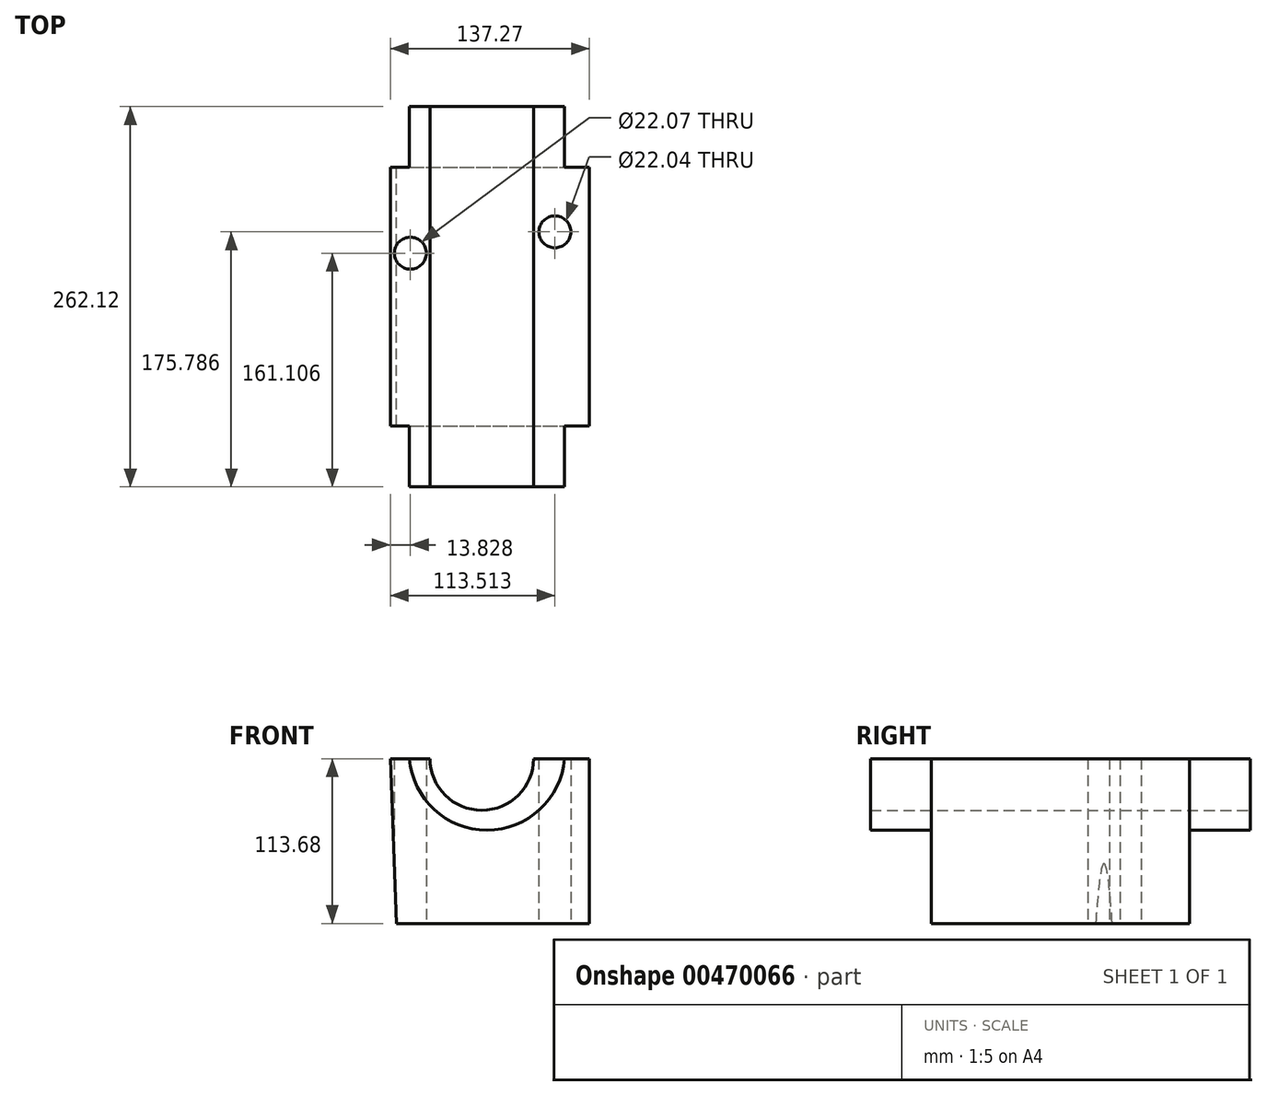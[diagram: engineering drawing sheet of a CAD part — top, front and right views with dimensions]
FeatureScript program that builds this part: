
annotation { "Feature Type Name" : "Feature", "Feature Type Description" : "" }
export const myFeature = defineFeature(function(context is Context, id is Id, definition is map)
    precondition{}
    {
        {
            var Q0;
            Q0=qCreatedBy(makeId("Front.planeOp"),FACE);
            var sketch = newSketch(context, id + "F0", { "sketchPlane" : qUnion([Q0])});
            skLineSegment(sketch, "E0", {"start": v(-69.6, -60) * mm, "end": v(63.28, -60) * mm});
            skLineSegment(sketch, "E1", {"start": v(63.28, -60) * mm, "end": v(63.28, 53.67) * mm});
            skLineSegment(sketch, "E2", {"start": v(63.28, 53.67) * mm, "end": v(24.9, 53.67) * mm});
            skLineSegment(sketch, "E3", {"start": v(-73.99, 53.67) * mm, "end": v(-69.6, -60) * mm});
            skArc(sketch, "E4", {"start": v(-46.69, 53.67) * mm, "mid": v(-10.9, 18.09) * mm, "end": v(24.9, 53.67) * mm});
            skArc(sketch, "E5", {"start": v(-60.81, 53.67) * mm, "mid": v(-7.3, 4.33) * mm, "end": v(46.22, 53.67) * mm});
            skLineSegment(sketch, "E6.trimOffspring", {"start": v(-46.69, 53.67) * mm, "end": v(-73.99, 53.67) * mm});
            skSolve(sketch);
        }
        {
            var Q0;
            Q0 = qSketchRegion(id + "F0", true);
            extrude(context, id + "F1", {"entities" : qUnion([Q0]), "endBound" : BoundingType.SYMMETRIC, "depth" : 178.3 * mm});
        }
        {
            var Q0;
            {var subQ0=sQuery(id+"F0.wireOp",EDGE,"E4");Q0=makeQuery(id+"F0.imprint","IMPRINT",FACE,{"disambiguationData":[TD([[makeQuery(id+"F0.imprint","IMPRINT",EDGE,{"derivedFrom":subQ0}),-1.0]])]});}
            extrude(context, id + "F2", {"entities" : qUnion([Q0]), "operationType" : NewBodyOperationType.ADD, "endBound" : BoundingType.SYMMETRIC, "depth" : 262.13 * mm});
        }
        {
            var Q0;
            Q0=qCreatedBy(makeId("Top.planeOp"),FACE);
            var sketch = newSketch(context, id + "F3", { "sketchPlane" : qUnion([Q0])});
            skCircle(sketch, "E7", {"center": v(39.52, 44.73) * mm, "radius": 11.02 * mm});
            skCircle(sketch, "E8", {"center": v(-60.16, 30.05) * mm, "radius": 11.03 * mm});
            skSolve(sketch);
        }
        {
            var Q0;
            Q0 = qSketchRegion(id + "F3", true);
            extrude(context, id + "F4", {"entities" : qUnion([Q0]), "operationType" : NewBodyOperationType.ADD, "depth" : 25.4 * mm});
        }
        {
            var Q0;
            Q0 = qSketchRegion(id + "F3", true);
            extrude(context, id + "F5", {"entities" : qUnion([Q0]), "operationType" : NewBodyOperationType.REMOVE, "endBound" : BoundingType.SYMMETRIC, "depth" : 277.88 * mm});
        }
    });
